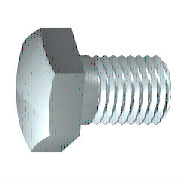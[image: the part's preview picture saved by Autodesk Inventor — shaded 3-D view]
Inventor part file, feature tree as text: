
AUTODESK INVENTOR PART (.ipt)
format: ipt  version: 2021 (Build 250183000, 183)  size: 191,488 bytes
history: native  units: mm (DEFAULTED — no unit token found)
features: sketch x3, extrude x1, chamfer x1, plane x1
ambient origin geometry x7: Origin, YZ Plane, XZ Plane, X Axis, Y Axis, Z Axis, Center Point
bodies: Solid1 (feature_tree), Body (feature_tree)
feature tree (6):
  extrude  "Head"  Depth=46.0mm
  chamfer  "Chamfer1"  Distance=11.7mm
  plane  "Work Plane1"
  sketch  "Sketch1"  dims[d0=100.0mm d1=46.0mm]
  sketch  "Sketch2"  dims[d2=20.0mm]
  sketch  "Sketch4"  dims[d12=90.0deg d3=11.7mm d4=0.0mm d5=30.0deg d21=90.0deg d6=1.2269mm d7=1.227mm d8=0.0mm d9=0.8001mm d10=28.19mm d11=30.0mm d13=1.227mm d14=20.0mm d15=46.0mm d16=0.0mm d19=30.0mm d55=45.0deg d57=0.0mm d58=0.0mm]
